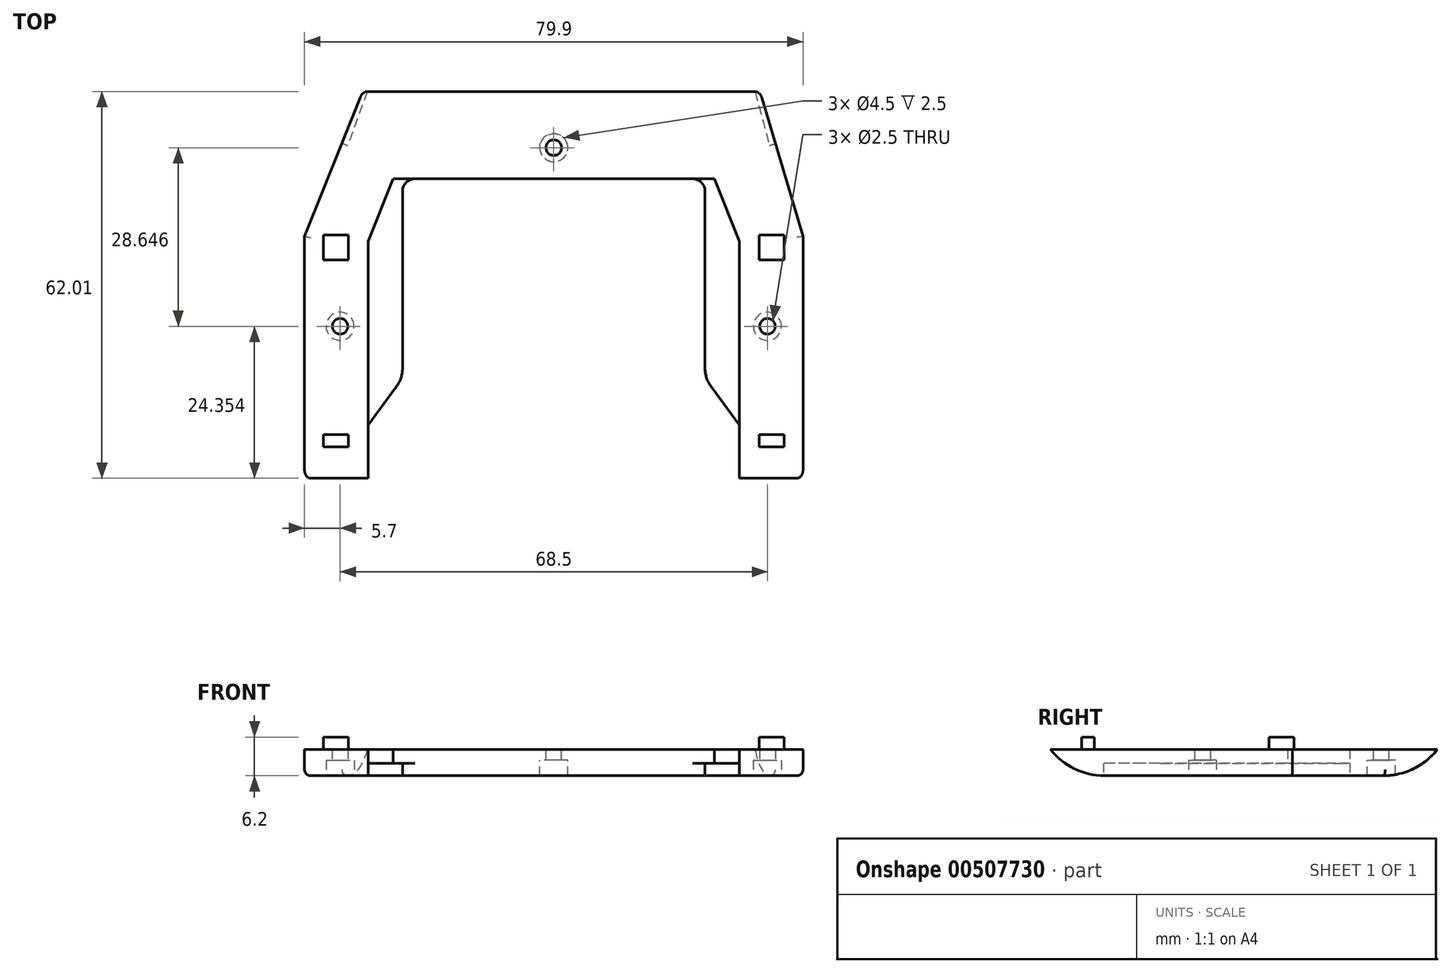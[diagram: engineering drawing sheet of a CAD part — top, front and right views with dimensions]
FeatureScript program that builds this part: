
annotation { "Feature Type Name" : "Feature", "Feature Type Description" : "" }
export const myFeature = defineFeature(function(context is Context, id is Id, definition is map)
    precondition{}
    {
        {
            var Q0;
            Q0=qCreatedBy(makeId("Top.planeOp"),FACE);
            var sketch = newSketch(context, id + "F0", { "sketchPlane" : qUnion([Q0])});
            skLineSegment(sketch, "E0.bottom", {"start": v(-25.5, 14.25) * mm, "end": v(26, 14.25) * mm});
            skLineSegment(sketch, "E0.left", {"start": v(-29.5, 4.25) * mm, "end": v(-29.5, -35.75) * mm});
            skLineSegment(sketch, "E0.right", {"start": v(30, 4.25) * mm, "end": v(30, -35.75) * mm});
            skLineSegment(sketch, "E1", {"start": v(-25.5, 14.25) * mm, "end": v(-29.5, 4.25) * mm});
            skPoint(sketch, "E2.orphan", {"position": v(-29.5, 14.25) * mm});
            skLineSegment(sketch, "E3", {"start": v(26, 14.25) * mm, "end": v(30, 4.25) * mm});
            skPoint(sketch, "E4.orphan", {"position": v(30, 14.25) * mm});
            skLineSegment(sketch, "E5.0", {"start": v(-24.2, 28.25) * mm, "end": v(-33.5, 5.02) * mm});
            skLineSegment(sketch, "E5.1", {"start": v(-33.5, -33.75) * mm, "end": v(34, -33.75) * mm});
            skLineSegment(sketch, "E5.2", {"start": v(34, 5.02) * mm, "end": v(34, -33.75) * mm});
            skLineSegment(sketch, "E5.3", {"start": v(-33.5, 5.02) * mm, "end": v(-33.5, -33.75) * mm});
            skLineSegment(sketch, "E5.4", {"start": v(27.1, 28.25) * mm, "end": v(34, 5.02) * mm});
            skLineSegment(sketch, "E5.5", {"start": v(-24.2, 28.25) * mm, "end": v(27.1, 28.25) * mm});
            skLineSegment(sketch, "E6", {"start": v(-29.5, -33.75) * mm, "end": v(-29.5, -35.75) * mm});
            skLineSegment(sketch, "E7", {"start": v(30, -33.75) * mm, "end": v(30, -35.75) * mm});
            skLineSegment(sketch, "E8.bottom", {"start": v(-29.5, -33.75) * mm, "end": v(30, -33.75) * mm});
            skLineSegment(sketch, "E8.left", {"start": v(-29.5, -33.75) * mm, "end": v(-29.5, -25.25) * mm});
            skLineSegment(sketch, "E8.right", {"start": v(30, -33.75) * mm, "end": v(30, -25.25) * mm});
            skLineSegment(sketch, "E9.top", {"start": v(-22, 14.25) * mm, "end": v(22.5, 14.25) * mm});
            skLineSegment(sketch, "E9.left", {"start": v(-24, -17.75) * mm, "end": v(-24, 12.25) * mm});
            skLineSegment(sketch, "E9.right", {"start": v(24.5, -17.75) * mm, "end": v(24.5, 12.25) * mm});
            skPoint(sketch, "E10.visualSharp", {"position": v(-24, 14.25) * mm});
            skArc(sketch, "E10.filletArc", {"start": v(-22, 14.25) * mm, "mid": v(-23.41, 13.66) * mm, "end": v(-24, 12.25) * mm});
            skPoint(sketch, "E11.visualSharp", {"position": v(24.5, 14.25) * mm});
            skArc(sketch, "E11.filletArc", {"start": v(24.5, 12.25) * mm, "mid": v(23.91, 13.66) * mm, "end": v(22.5, 14.25) * mm});
            skLineSegment(sketch, "E12", {"start": v(24.5, -17.75) * mm, "end": v(30, -25.25) * mm});
            skLineSegment(sketch, "E13", {"start": v(-24, -17.75) * mm, "end": v(-29.5, -25.25) * mm});
            skPoint(sketch, "E14.orphan", {"position": v(-29.5, -16.75) * mm});
            skPoint(sketch, "E15.orphan", {"position": v(30, -16.75) * mm});
            skSolve(sketch);
        }
        {
            var Q0;
            Q0=makeQuery(id+"F0.imprint","IMPRINT",FACE,{"disambiguationData":[TD([[makeQuery(id+"F0.imprint","IMPRINT",EDGE,{"derivedFrom":sQuery(id+"F0.wireOp",EDGE,"E0.bottom")}),-1.0]])]});
            extrude(context, id + "F1", {"entities" : qUnion([Q0]), "depth" : 2 * mm, "offsetDistance" : 25 * mm});
        }
        {
            var Q0;
            Q0=makeQuery(id+"F0.imprint","IMPRINT",FACE,{"disambiguationData":[TD([[makeQuery(id+"F0.imprint","IMPRINT",EDGE,{"derivedFrom":sQuery(id+"F0.wireOp",EDGE,"E0.bottom")}),1.0]])]});
            extrude(context, id + "F2", {"entities" : qUnion([Q0]), "operationType" : NewBodyOperationType.ADD, "depth" : 4.2 * mm, "offsetDistance" : 25 * mm});
        }
        {
            var Q0;
            {var subQ0=sQuery(id+"F0.wireOp",EDGE,"E5.1");Q0=makeQuery(id+"F2.opExtrude","CAP_EDGE",EDGE,{"disambiguationData":[OSD([subQ0]),TDD([makeQuery(id+"F0.imprint","IMPRINT",EDGE,{"disambiguationData":[TD([[makeQuery(id+"F0.imprint","INTERSECT",VERTEX,{"derivedFrom":[subQ0,sQuery(id+"F0.wireOp",EDGE,"E5.2")]}),1.0]])],"derivedFrom":subQ0})])],"isStart":true});}
            var Q1;
            Q1=makeQuery(id+"F2.opExtrude","CAP_EDGE",EDGE,{"disambiguationData":[OSD([sQuery(id+"F0.wireOp",EDGE,"E5.5")])],"isStart":true});
            var Q2;
            {var subQ0=sQuery(id+"F0.wireOp",EDGE,"E5.1");Q2=makeQuery(id+"F2.opExtrude","CAP_EDGE",EDGE,{"disambiguationData":[OSD([subQ0]),TDD([makeQuery(id+"F0.imprint","IMPRINT",EDGE,{"disambiguationData":[TD([[makeQuery(id+"F0.imprint","INTERSECT",VERTEX,{"derivedFrom":[subQ0,sQuery(id+"F0.wireOp",EDGE,"E5.3")]}),-1.0]])],"derivedFrom":subQ0})])],"isStart":true});}
            fillet(context, id + "F3", {"entities" : qUnion([Q0, Q1, Q2]), "radius" : 11 * mm, "tangentPropagation" : true, "allowEdgeOverflow" : false});
        }
        {
            var Q0;
            Q0=makeQuery(id+"F2.opExtrude","SWEPT_FACE",FACE,{"disambiguationData":[OSD([sQuery(id+"F0.wireOp",EDGE,"E5.3")])]});
            var Q1;
            Q1=makeQuery(id+"F2.opExtrude","SWEPT_FACE",FACE,{"disambiguationData":[OSD([sQuery(id+"F0.wireOp",EDGE,"E5.0")])]});
            extrude(context, id + "F4", {"entities" : qUnion([Q0, Q1]), "operationType" : NewBodyOperationType.ADD, "depth" : 6.2 * mm, "offsetDistance" : 25 * mm});
        }
        {
            var Q0;
            {var subQ0=sQuery(id+"F0.wireOp",EDGE,"E5.3");Q0=makeQuery(id+"F4.opExtrude","CAP_EDGE",EDGE,{"disambiguationData":[OSD([subQ0]),TDD([makeQuery(id+"F2.opExtrude","CAP_EDGE",EDGE,{"disambiguationData":[OSD([subQ0])],"isStart":true})])],"isStart":false});}
            var Q1;
            Q1=makeQuery(id+"F4.opExtrude","CAP_EDGE",EDGE,{"disambiguationData":[OSD([sQuery(id+"F0.wireOp",EDGE,"E5.0"),sQuery(id+"F0.wireOp",EDGE,"E5.5")]),OD(0.0)],"isStart":false});
            fillet(context, id + "F5", {"entities" : qUnion([Q0, Q1]), "radius" : 1 * mm, "tangentPropagation" : true, "allowEdgeOverflow" : false});
        }
        {
            var Q0;
            Q0=makeQuery(id+"F2.opExtrude","SWEPT_FACE",FACE,{"disambiguationData":[OSD([sQuery(id+"F0.wireOp",EDGE,"E5.2")])]});
            var Q1;
            Q1=makeQuery(id+"F2.opExtrude","SWEPT_FACE",FACE,{"disambiguationData":[OSD([sQuery(id+"F0.wireOp",EDGE,"E5.4")])]});
            extrude(context, id + "F6", {"entities" : qUnion([Q0, Q1]), "operationType" : NewBodyOperationType.ADD, "depth" : 6.2 * mm, "offsetDistance" : 25 * mm});
        }
        {
            var Q0;
            {var subQ0=sQuery(id+"F0.wireOp",EDGE,"E5.4");Q0=makeQuery(id+"F6.opExtrude","CAP_EDGE",EDGE,{"disambiguationData":[OSD([subQ0]),TDD([makeQuery(id+"F2.opExtrude","CAP_EDGE",EDGE,{"disambiguationData":[OSD([subQ0])],"isStart":true})]),OD(1.0)],"isStart":false});}
            var Q1;
            {var subQ0=sQuery(id+"F0.wireOp",EDGE,"E5.2");Q1=makeQuery(id+"F6.opExtrude","CAP_EDGE",EDGE,{"disambiguationData":[OSD([subQ0]),TDD([makeQuery(id+"F2.opExtrude","CAP_EDGE",EDGE,{"disambiguationData":[OSD([subQ0])],"isStart":true})])],"isStart":false});}
            fillet(context, id + "F7", {"entities" : qUnion([Q0, Q1]), "radius" : 1 * mm, "tangentPropagation" : true, "allowEdgeOverflow" : false});
        }
        {
            var Q0;
            {var subQ0=sQuery(id+"F0.wireOp",EDGE,"E5.4");var subQ1=sQuery(id+"F0.wireOp",EDGE,"E5.2");var subQ2=sQuery(id+"F0.wireOp",EDGE,"E5.3");var subQ3=sQuery(id+"F0.wireOp",EDGE,"E5.0");Q0=makeQuery(id+"F6.boolean.opBoolean","MERGE",FACE,{"derivedFrom":[makeQuery(id+"F4.boolean.opBoolean","MERGE",FACE,{"derivedFrom":[makeQuery(id+"F2.opExtrude","CAP_FACE",FACE,{"disambiguationData":[OSD([sQuery(id+"F0.wireOp",EDGE,"E0.bottom"),sQuery(id+"F0.wireOp",EDGE,"E0.left"),sQuery(id+"F0.wireOp",EDGE,"E0.right"),sQuery(id+"F0.wireOp",EDGE,"E1"),sQuery(id+"F0.wireOp",EDGE,"E3"),subQ3,sQuery(id+"F0.wireOp",EDGE,"E5.1"),subQ1,subQ2,subQ0,sQuery(id+"F0.wireOp",EDGE,"E5.5"),sQuery(id+"F0.wireOp",EDGE,"E8.left"),sQuery(id+"F0.wireOp",EDGE,"E8.right"),sQuery(id+"F0.wireOp",EDGE,"E9.top")])],"isStart":false}),makeQuery(id+"F4.opExtrude","SWEPT_FACE",FACE,{"disambiguationData":[OSD([subQ3]),TDD([makeQuery(id+"F2.opExtrude","CAP_EDGE",EDGE,{"disambiguationData":[OSD([subQ3])],"isStart":false})])]}),makeQuery(id+"F4.opExtrude","SWEPT_FACE",FACE,{"disambiguationData":[OSD([subQ2]),TDD([makeQuery(id+"F2.opExtrude","CAP_EDGE",EDGE,{"disambiguationData":[OSD([subQ2])],"isStart":false})])]})]}),makeQuery(id+"F6.opExtrude","SWEPT_FACE",FACE,{"disambiguationData":[OSD([subQ1]),TDD([makeQuery(id+"F2.opExtrude","CAP_EDGE",EDGE,{"disambiguationData":[OSD([subQ1])],"isStart":false})])]}),makeQuery(id+"F6.opExtrude","SWEPT_FACE",FACE,{"disambiguationData":[OSD([subQ0]),TDD([makeQuery(id+"F2.opExtrude","CAP_EDGE",EDGE,{"disambiguationData":[OSD([subQ0])],"isStart":false})])]})]});}
            var sketch = newSketch(context, id + "F8", { "sketchPlane" : qUnion([Q0])});
            skLineSegment(sketch, "E16.bottom", {"start": v(-36.7, -28.75) * mm, "end": v(-32.7, -28.75) * mm});
            skLineSegment(sketch, "E16.top", {"start": v(-36.7, -26.75) * mm, "end": v(-32.7, -26.75) * mm});
            skLineSegment(sketch, "E16.left", {"start": v(-36.7, -28.75) * mm, "end": v(-36.7, -26.75) * mm});
            skLineSegment(sketch, "E16.right", {"start": v(-32.7, -28.75) * mm, "end": v(-32.7, -26.75) * mm});
            skLineSegment(sketch, "E17.bottom", {"start": v(37.2, -28.75) * mm, "end": v(33.2, -28.75) * mm});
            skLineSegment(sketch, "E17.top", {"start": v(37.2, -26.75) * mm, "end": v(33.2, -26.75) * mm});
            skLineSegment(sketch, "E17.left", {"start": v(37.2, -28.75) * mm, "end": v(37.2, -26.75) * mm});
            skLineSegment(sketch, "E17.right", {"start": v(33.2, -28.75) * mm, "end": v(33.2, -26.75) * mm});
            skLineSegment(sketch, "E18.bottom", {"start": v(33.2, 1.25) * mm, "end": v(37.2, 1.25) * mm});
            skLineSegment(sketch, "E18.top", {"start": v(33.2, 5.25) * mm, "end": v(37.2, 5.25) * mm});
            skLineSegment(sketch, "E18.left", {"start": v(33.2, 1.25) * mm, "end": v(33.2, 5.25) * mm});
            skLineSegment(sketch, "E18.right", {"start": v(37.2, 1.25) * mm, "end": v(37.2, 5.25) * mm});
            skLineSegment(sketch, "E19.bottom", {"start": v(-36.7, 1.25) * mm, "end": v(-32.7, 1.25) * mm});
            skLineSegment(sketch, "E19.top", {"start": v(-36.7, 5.25) * mm, "end": v(-32.7, 5.25) * mm});
            skLineSegment(sketch, "E19.left", {"start": v(-36.7, 1.25) * mm, "end": v(-36.7, 5.25) * mm});
            skLineSegment(sketch, "E19.right", {"start": v(-32.7, 1.25) * mm, "end": v(-32.7, 5.25) * mm});
            skSolve(sketch);
        }
        {
            var Q0;
            Q0 = qSketchRegion(id + "F8", true);
            extrude(context, id + "F9", {"entities" : qUnion([Q0]), "operationType" : NewBodyOperationType.ADD, "depth" : 2 * mm, "offsetDistance" : 25 * mm});
        }
        {
            var Q0;
            {var subQ0=sQuery(id+"F0.wireOp",EDGE,"E5.3");var subQ1=sQuery(id+"F0.wireOp",EDGE,"E5.0");var subQ2=sQuery(id+"F0.wireOp",EDGE,"E3");var subQ3=sQuery(id+"F0.wireOp",EDGE,"E1");var subQ4=sQuery(id+"F0.wireOp",EDGE,"E0.right");var subQ5=sQuery(id+"F0.wireOp",EDGE,"E0.left");var subQ6=sQuery(id+"F0.wireOp",EDGE,"E0.bottom");Q0=makeQuery(id+"F4.boolean.opBoolean","MERGE",FACE,{"derivedFrom":[makeQuery(id+"F3.opFillet","SPLIT",FACE,{"disambiguationData":[OD(0.0)],"derivedFrom":makeQuery(id+"F2.boolean.opBoolean","MERGE",FACE,{"derivedFrom":[makeQuery(id+"F1.opExtrude","CAP_FACE",FACE,{"disambiguationData":[OSD([subQ6,subQ5,subQ3,sQuery(id+"F0.wireOp",EDGE,"E9.left"),sQuery(id+"F0.wireOp",EDGE,"E10.filletArc"),sQuery(id+"F0.wireOp",EDGE,"E13")])],"isStart":true}),makeQuery(id+"F1.opExtrude","CAP_FACE",FACE,{"disambiguationData":[OSD([subQ6,subQ4,subQ2,sQuery(id+"F0.wireOp",EDGE,"E9.right"),sQuery(id+"F0.wireOp",EDGE,"E11.filletArc"),sQuery(id+"F0.wireOp",EDGE,"E12")])],"isStart":true}),makeQuery(id+"F2.opExtrude","CAP_FACE",FACE,{"disambiguationData":[OSD([subQ6,subQ5,subQ4,subQ3,subQ2,subQ1,sQuery(id+"F0.wireOp",EDGE,"E5.1"),sQuery(id+"F0.wireOp",EDGE,"E5.2"),subQ0,sQuery(id+"F0.wireOp",EDGE,"E5.4"),sQuery(id+"F0.wireOp",EDGE,"E5.5"),sQuery(id+"F0.wireOp",EDGE,"E8.left"),sQuery(id+"F0.wireOp",EDGE,"E8.right"),sQuery(id+"F0.wireOp",EDGE,"E9.top")])],"isStart":true})]})}),makeQuery(id+"F4.opExtrude","SWEPT_FACE",FACE,{"disambiguationData":[OSD([subQ1]),TDD([makeQuery(id+"F2.opExtrude","CAP_EDGE",EDGE,{"disambiguationData":[OSD([subQ1])],"isStart":true})])]}),makeQuery(id+"F4.opExtrude","SWEPT_FACE",FACE,{"disambiguationData":[OSD([subQ0]),TDD([makeQuery(id+"F2.opExtrude","CAP_EDGE",EDGE,{"disambiguationData":[OSD([subQ0])],"isStart":true})])]})]});}
            var sketch = newSketch(context, id + "F10", { "sketchPlane" : qUnion([Q0])});
            skCircle(sketch, "E20", {"center": v(-34, 9.4) * mm, "radius": 2.25 * mm});
            skCircle(sketch, "E21", {"center": v(34.5, 9.4) * mm, "radius": 2.25 * mm});
            skCircle(sketch, "E22", {"center": v(-34, 9.4) * mm, "radius": 1.25 * mm});
            skCircle(sketch, "E23", {"center": v(34.5, 9.4) * mm, "radius": 1.25 * mm});
            skSolve(sketch);
        }
        {
            var Q0;
            Q0 = qSketchRegion(id + "F10", true);
            extrude(context, id + "F11", {"entities" : qUnion([Q0]), "operationType" : NewBodyOperationType.REMOVE, "oppositeDirection" : true, "depth" : 2.5 * mm, "offsetDistance" : 25 * mm});
        }
        {
            var Q0;
            {var subQ0=sQuery(id+"F0.wireOp",EDGE,"E5.3");var subQ1=sQuery(id+"F0.wireOp",EDGE,"E5.0");var subQ2=sQuery(id+"F0.wireOp",EDGE,"E3");var subQ3=sQuery(id+"F0.wireOp",EDGE,"E1");var subQ4=sQuery(id+"F0.wireOp",EDGE,"E0.right");var subQ5=sQuery(id+"F0.wireOp",EDGE,"E0.left");var subQ6=sQuery(id+"F0.wireOp",EDGE,"E0.bottom");Q0=makeQuery(id+"F11.boolean.opBoolean","SPLIT",FACE,{"disambiguationData":[TD([makeQuery(id+"F11.opExtrude","SWEPT_FACE",FACE,{"disambiguationData":[OSD([sQuery(id+"F10.wireOp",EDGE,"E22")])]})])],"derivedFrom":makeQuery(id+"F4.boolean.opBoolean","MERGE",FACE,{"derivedFrom":[makeQuery(id+"F3.opFillet","SPLIT",FACE,{"disambiguationData":[OD(0.0)],"derivedFrom":makeQuery(id+"F2.boolean.opBoolean","MERGE",FACE,{"derivedFrom":[makeQuery(id+"F1.opExtrude","CAP_FACE",FACE,{"disambiguationData":[OSD([subQ6,subQ5,subQ3,sQuery(id+"F0.wireOp",EDGE,"E9.left"),sQuery(id+"F0.wireOp",EDGE,"E10.filletArc"),sQuery(id+"F0.wireOp",EDGE,"E13")])],"isStart":true}),makeQuery(id+"F1.opExtrude","CAP_FACE",FACE,{"disambiguationData":[OSD([subQ6,subQ4,subQ2,sQuery(id+"F0.wireOp",EDGE,"E9.right"),sQuery(id+"F0.wireOp",EDGE,"E11.filletArc"),sQuery(id+"F0.wireOp",EDGE,"E12")])],"isStart":true}),makeQuery(id+"F2.opExtrude","CAP_FACE",FACE,{"disambiguationData":[OSD([subQ6,subQ5,subQ4,subQ3,subQ2,subQ1,sQuery(id+"F0.wireOp",EDGE,"E5.1"),sQuery(id+"F0.wireOp",EDGE,"E5.2"),subQ0,sQuery(id+"F0.wireOp",EDGE,"E5.4"),sQuery(id+"F0.wireOp",EDGE,"E5.5"),sQuery(id+"F0.wireOp",EDGE,"E8.left"),sQuery(id+"F0.wireOp",EDGE,"E8.right"),sQuery(id+"F0.wireOp",EDGE,"E9.top")])],"isStart":true})]})}),makeQuery(id+"F4.opExtrude","SWEPT_FACE",FACE,{"disambiguationData":[OSD([subQ1]),TDD([makeQuery(id+"F2.opExtrude","CAP_EDGE",EDGE,{"disambiguationData":[OSD([subQ1])],"isStart":true})])]}),makeQuery(id+"F4.opExtrude","SWEPT_FACE",FACE,{"disambiguationData":[OSD([subQ0]),TDD([makeQuery(id+"F2.opExtrude","CAP_EDGE",EDGE,{"disambiguationData":[OSD([subQ0])],"isStart":true})])]})]})});}
            var Q1;
            {var subQ0=sQuery(id+"F0.wireOp",EDGE,"E5.2");var subQ1=sQuery(id+"F0.wireOp",EDGE,"E5.4");var subQ2=sQuery(id+"F0.wireOp",EDGE,"E3");var subQ3=sQuery(id+"F0.wireOp",EDGE,"E1");var subQ4=sQuery(id+"F0.wireOp",EDGE,"E0.right");var subQ5=sQuery(id+"F0.wireOp",EDGE,"E0.left");var subQ6=sQuery(id+"F0.wireOp",EDGE,"E0.bottom");Q1=makeQuery(id+"F11.boolean.opBoolean","SPLIT",FACE,{"disambiguationData":[TD([makeQuery(id+"F11.opExtrude","SWEPT_FACE",FACE,{"disambiguationData":[OSD([sQuery(id+"F10.wireOp",EDGE,"E23")])]})])],"derivedFrom":makeQuery(id+"F6.boolean.opBoolean","MERGE",FACE,{"derivedFrom":[makeQuery(id+"F3.opFillet","SPLIT",FACE,{"disambiguationData":[OD(1.0)],"derivedFrom":makeQuery(id+"F2.boolean.opBoolean","MERGE",FACE,{"derivedFrom":[makeQuery(id+"F1.opExtrude","CAP_FACE",FACE,{"disambiguationData":[OSD([subQ6,subQ5,subQ3,sQuery(id+"F0.wireOp",EDGE,"E9.left"),sQuery(id+"F0.wireOp",EDGE,"E10.filletArc"),sQuery(id+"F0.wireOp",EDGE,"E13")])],"isStart":true}),makeQuery(id+"F1.opExtrude","CAP_FACE",FACE,{"disambiguationData":[OSD([subQ6,subQ4,subQ2,sQuery(id+"F0.wireOp",EDGE,"E9.right"),sQuery(id+"F0.wireOp",EDGE,"E11.filletArc"),sQuery(id+"F0.wireOp",EDGE,"E12")])],"isStart":true}),makeQuery(id+"F2.opExtrude","CAP_FACE",FACE,{"disambiguationData":[OSD([subQ6,subQ5,subQ4,subQ3,subQ2,sQuery(id+"F0.wireOp",EDGE,"E5.0"),sQuery(id+"F0.wireOp",EDGE,"E5.1"),subQ0,sQuery(id+"F0.wireOp",EDGE,"E5.3"),subQ1,sQuery(id+"F0.wireOp",EDGE,"E5.5"),sQuery(id+"F0.wireOp",EDGE,"E8.left"),sQuery(id+"F0.wireOp",EDGE,"E8.right"),sQuery(id+"F0.wireOp",EDGE,"E9.top")])],"isStart":true})]})}),makeQuery(id+"F6.opExtrude","SWEPT_FACE",FACE,{"disambiguationData":[OSD([subQ1]),TDD([makeQuery(id+"F2.opExtrude","CAP_EDGE",EDGE,{"disambiguationData":[OSD([subQ1])],"isStart":true})])]}),makeQuery(id+"F6.opExtrude","SWEPT_FACE",FACE,{"disambiguationData":[OSD([subQ0]),TDD([makeQuery(id+"F2.opExtrude","CAP_EDGE",EDGE,{"disambiguationData":[OSD([subQ0])],"isStart":true})])]})]})});}
            extrude(context, id + "F12", {"entities" : qUnion([Q0, Q1]), "operationType" : NewBodyOperationType.REMOVE, "oppositeDirection" : true, "depth" : 4.5 * mm, "offsetDistance" : 25 * mm});
        }
        {
            var Q0;
            Q0=makeQuery(id+"F1.opExtrude","SWEPT_EDGE",EDGE,{"disambiguationData":[OSD([sQuery(id+"F0.wireOp",EDGE,"E9.right"),sQuery(id+"F0.wireOp",EDGE,"E12")])]});
            var Q1;
            Q1=makeQuery(id+"F1.opExtrude","SWEPT_EDGE",EDGE,{"disambiguationData":[OSD([sQuery(id+"F0.wireOp",EDGE,"E9.left"),sQuery(id+"F0.wireOp",EDGE,"E13")])]});
            fillet(context, id + "F13", {"entities" : qUnion([Q0, Q1]), "radius" : 5 * mm, "tangentPropagation" : true, "allowEdgeOverflow" : false});
        }
        {
            var Q0;
            {var subQ0=sQuery(id+"F0.wireOp",EDGE,"E5.4");var subQ1=sQuery(id+"F0.wireOp",EDGE,"E5.2");var subQ2=sQuery(id+"F0.wireOp",EDGE,"E5.3");var subQ3=sQuery(id+"F0.wireOp",EDGE,"E5.0");Q0=makeQuery(id+"F6.boolean.opBoolean","MERGE",FACE,{"derivedFrom":[makeQuery(id+"F4.boolean.opBoolean","MERGE",FACE,{"derivedFrom":[makeQuery(id+"F2.opExtrude","CAP_FACE",FACE,{"disambiguationData":[OSD([sQuery(id+"F0.wireOp",EDGE,"E0.bottom"),sQuery(id+"F0.wireOp",EDGE,"E0.left"),sQuery(id+"F0.wireOp",EDGE,"E0.right"),sQuery(id+"F0.wireOp",EDGE,"E1"),sQuery(id+"F0.wireOp",EDGE,"E3"),subQ3,sQuery(id+"F0.wireOp",EDGE,"E5.1"),subQ1,subQ2,subQ0,sQuery(id+"F0.wireOp",EDGE,"E5.5"),sQuery(id+"F0.wireOp",EDGE,"E8.left"),sQuery(id+"F0.wireOp",EDGE,"E8.right"),sQuery(id+"F0.wireOp",EDGE,"E9.top")])],"isStart":false}),makeQuery(id+"F4.opExtrude","SWEPT_FACE",FACE,{"disambiguationData":[OSD([subQ3]),TDD([makeQuery(id+"F2.opExtrude","CAP_EDGE",EDGE,{"disambiguationData":[OSD([subQ3])],"isStart":false})])]}),makeQuery(id+"F4.opExtrude","SWEPT_FACE",FACE,{"disambiguationData":[OSD([subQ2]),TDD([makeQuery(id+"F2.opExtrude","CAP_EDGE",EDGE,{"disambiguationData":[OSD([subQ2])],"isStart":false})])]})]}),makeQuery(id+"F6.opExtrude","SWEPT_FACE",FACE,{"disambiguationData":[OSD([subQ1]),TDD([makeQuery(id+"F2.opExtrude","CAP_EDGE",EDGE,{"disambiguationData":[OSD([subQ1])],"isStart":false})])]}),makeQuery(id+"F6.opExtrude","SWEPT_FACE",FACE,{"disambiguationData":[OSD([subQ0]),TDD([makeQuery(id+"F2.opExtrude","CAP_EDGE",EDGE,{"disambiguationData":[OSD([subQ0])],"isStart":false})])]})]});}
            var sketch = newSketch(context, id + "F14", { "sketchPlane" : qUnion([Q0])});
            skCircle(sketch, "E24", {"center": v(0.25, 19.25) * mm, "radius": 1.25 * mm});
            skCircle(sketch, "E25", {"center": v(0.25, 19.25) * mm, "radius": 2.25 * mm});
            skSolve(sketch);
        }
        {
            var Q0;
            Q0 = qSketchRegion(id + "F14", true);
            extrude(context, id + "F15", {"entities" : qUnion([Q0]), "operationType" : NewBodyOperationType.REMOVE, "oppositeDirection" : true, "depth" : 6.8 * mm, "offsetDistance" : 25 * mm, "hasSecondDirection" : true, "secondDirectionOppositeDirection" : true, "secondDirectionDepth" : 1.7 * mm});
        }
        {
            var Q0;
            Q0=makeQuery(id+"F14.imprint","IMPRINT",FACE,{"disambiguationData":[TD([[makeQuery(id+"F14.imprint","IMPRINT",EDGE,{"derivedFrom":sQuery(id+"F14.wireOp",EDGE,"E24")}),1.0]])]});
            extrude(context, id + "F16", {"entities" : qUnion([Q0]), "operationType" : NewBodyOperationType.REMOVE, "oppositeDirection" : true, "depth" : 4.2 * mm, "offsetDistance" : 25 * mm});
        }
    });
